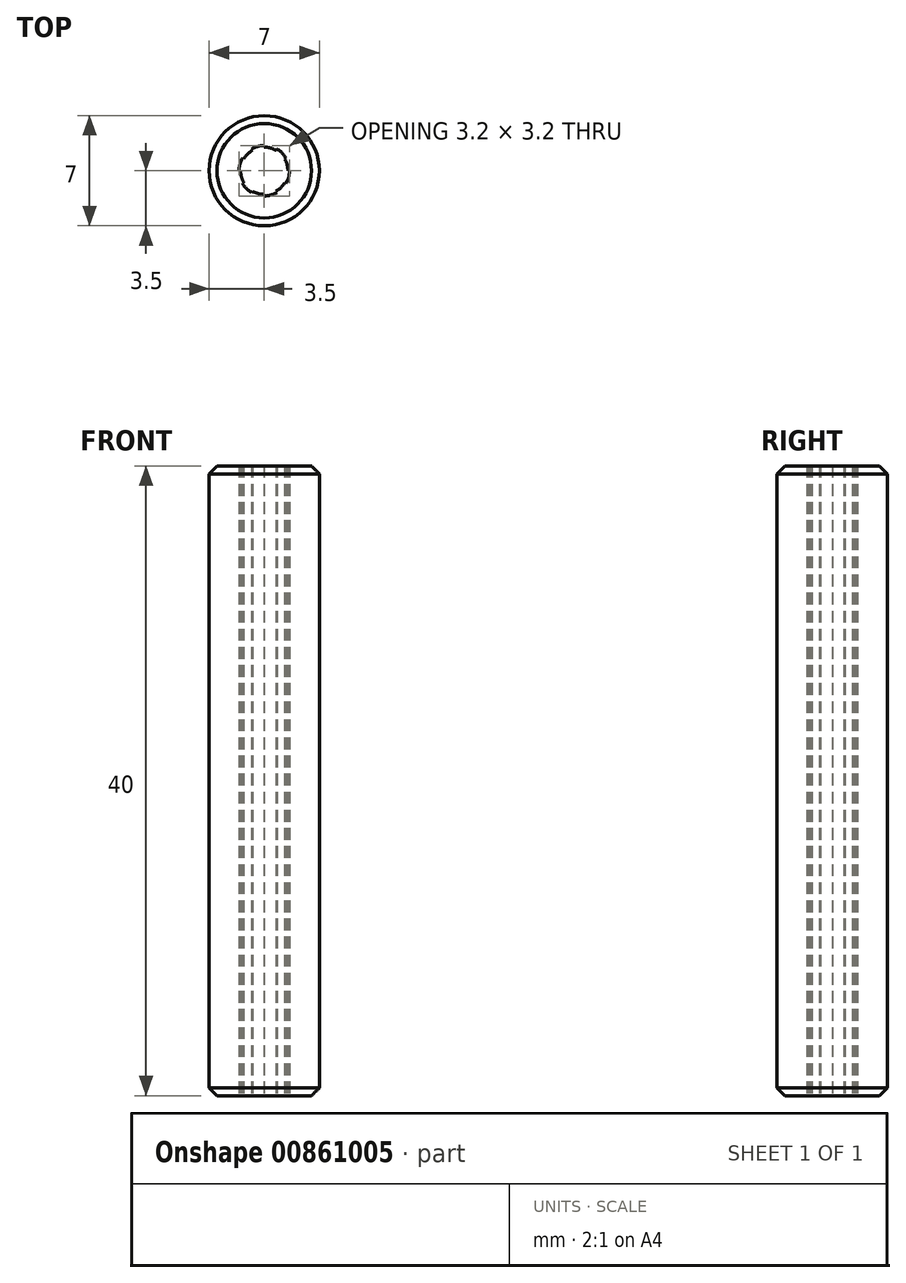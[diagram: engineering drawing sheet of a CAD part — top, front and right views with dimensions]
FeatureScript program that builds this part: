
annotation { "Feature Type Name" : "Feature", "Feature Type Description" : "" }
export const myFeature = defineFeature(function(context is Context, id is Id, definition is map)
    precondition{}
    {
        {
            var Q0;
            Q0=qCreatedBy(makeId("Top.planeOp"),FACE);
            var sketch = newSketch(context, id + "F0", { "sketchPlane" : qUnion([Q0])});
            skArc(sketch, "E0", {"start": v(-0.75, 1.3) * mm, "mid": v(-1.06, 1.06) * mm, "end": v(-1.3, 0.75) * mm});
            skCircle(sketch, "E1", {"center": v(0, 0) * mm, "radius": 3.5 * mm});
            skCircle(sketch, "E2.0", {"center": v(0, 0) * mm, "radius": 1.6 * mm});
            skLineSegment(sketch, "E3", {"start": v(0, 0) * mm, "end": v(0, 1.6) * mm, "construction": true});
            skLineSegment(sketch, "E4", {"start": v(0, 0) * mm, "end": v(-0.8, 1.39) * mm, "construction": true});
            skLineSegment(sketch, "E5", {"start": v(0, 0) * mm, "end": v(-1.39, 0.8) * mm, "construction": true});
            skLineSegment(sketch, "E6", {"start": v(0, 0) * mm, "end": v(-1.6, 0) * mm, "construction": true});
            skLineSegment(sketch, "E7", {"start": v(-1.3, 0.75) * mm, "end": v(-1.39, 0.8) * mm});
            skLineSegment(sketch, "E8", {"start": v(-0.75, 1.3) * mm, "end": v(-0.8, 1.39) * mm});
            skArc(sketch, "E9.1.0", {"start": v(-1.5, 0) * mm, "mid": v(-1.45, -0.39) * mm, "end": v(-1.3, -0.75) * mm});
            skArc(sketch, "E9.2.0", {"start": v(-0.75, -1.3) * mm, "mid": v(-0.39, -1.45) * mm, "end": v(0, -1.5) * mm});
            skArc(sketch, "E9.3.0", {"start": v(0.75, -1.3) * mm, "mid": v(1.06, -1.06) * mm, "end": v(1.3, -0.75) * mm});
            skArc(sketch, "E9.4.0", {"start": v(1.5, 0) * mm, "mid": v(1.45, 0.39) * mm, "end": v(1.3, 0.75) * mm});
            skArc(sketch, "E9.5.0", {"start": v(0.75, 1.3) * mm, "mid": v(0.39, 1.45) * mm, "end": v(0, 1.5) * mm});
            skLineSegment(sketch, "E10", {"start": v(-1.5, 0) * mm, "end": v(-1.6, 0) * mm});
            skLineSegment(sketch, "E11", {"start": v(-1.3, -0.75) * mm, "end": v(-1.39, -0.8) * mm});
            skLineSegment(sketch, "E12", {"start": v(0, 1.5) * mm, "end": v(0, 1.6) * mm});
            skLineSegment(sketch, "E13", {"start": v(0.75, 1.3) * mm, "end": v(0.8, 1.39) * mm});
            skLineSegment(sketch, "E14", {"start": v(1.3, 0.75) * mm, "end": v(1.39, 0.8) * mm});
            skLineSegment(sketch, "E15", {"start": v(1.6, 0) * mm, "end": v(1.5, 0) * mm});
            skLineSegment(sketch, "E16", {"start": v(1.39, -0.8) * mm, "end": v(1.3, -0.75) * mm});
            skLineSegment(sketch, "E17", {"start": v(0.75, -1.3) * mm, "end": v(0.8, -1.39) * mm});
            skLineSegment(sketch, "E18", {"start": v(0, -1.5) * mm, "end": v(0, -1.6) * mm});
            skLineSegment(sketch, "E19", {"start": v(-0.75, -1.3) * mm, "end": v(-0.8, -1.39) * mm});
            skSolve(sketch);
        }
        {
            var Q0;
            Q0=makeQuery(id+"F0.imprint","IMPRINT",FACE,{"disambiguationData":[TD([[makeQuery(id+"F0.imprint","IMPRINT",EDGE,{"derivedFrom":sQuery(id+"F0.wireOp",EDGE,"E0")}),-1.0]])]});
            var Q1;
            Q1=makeQuery(id+"F0.imprint","IMPRINT",FACE,{"disambiguationData":[TD([[makeQuery(id+"F0.imprint","IMPRINT",EDGE,{"derivedFrom":sQuery(id+"F0.wireOp",EDGE,"E9.1.0")}),-1.0]])]});
            var Q2;
            Q2=makeQuery(id+"F0.imprint","IMPRINT",FACE,{"disambiguationData":[TD([[makeQuery(id+"F0.imprint","IMPRINT",EDGE,{"derivedFrom":sQuery(id+"F0.wireOp",EDGE,"E9.2.0")}),-1.0]])]});
            var Q3;
            Q3=makeQuery(id+"F0.imprint","IMPRINT",FACE,{"disambiguationData":[TD([[makeQuery(id+"F0.imprint","IMPRINT",EDGE,{"derivedFrom":sQuery(id+"F0.wireOp",EDGE,"E9.3.0")}),-1.0]])]});
            var Q4;
            Q4=makeQuery(id+"F0.imprint","IMPRINT",FACE,{"disambiguationData":[TD([[makeQuery(id+"F0.imprint","IMPRINT",EDGE,{"derivedFrom":sQuery(id+"F0.wireOp",EDGE,"E9.4.0")}),-1.0]])]});
            var Q5;
            Q5=makeQuery(id+"F0.imprint","IMPRINT",FACE,{"disambiguationData":[TD([[makeQuery(id+"F0.imprint","IMPRINT",EDGE,{"derivedFrom":sQuery(id+"F0.wireOp",EDGE,"E9.5.0")}),-1.0]])]});
            var Q6;
            Q6=makeQuery(id+"F0.imprint","IMPRINT",FACE,{"disambiguationData":[TD([[makeQuery(id+"F0.imprint","IMPRINT",EDGE,{"derivedFrom":sQuery(id+"F0.wireOp",EDGE,"E1")}),1.0]])]});
            extrude(context, id + "F1", {"entities" : qUnion([Q0, Q1, Q2, Q3, Q4, Q5, Q6]), "depth" : 40 * mm, "offsetDistance" : 25 * mm});
        }
        {
            var Q0;
            Q0=makeQuery(id+"F1.opExtrude","CAP_EDGE",EDGE,{"disambiguationData":[OSD([sQuery(id+"F0.wireOp",EDGE,"E1")])],"isStart":false});
            var Q1;
            Q1=makeQuery(id+"F1.opExtrude","CAP_EDGE",EDGE,{"disambiguationData":[OSD([sQuery(id+"F0.wireOp",EDGE,"E1")])],"isStart":true});
            chamfer(context, id + "F2", {"entities" : qUnion([Q0, Q1]), "width" : 0.5 * mm, "tangentPropagation" : true});
        }
    });
